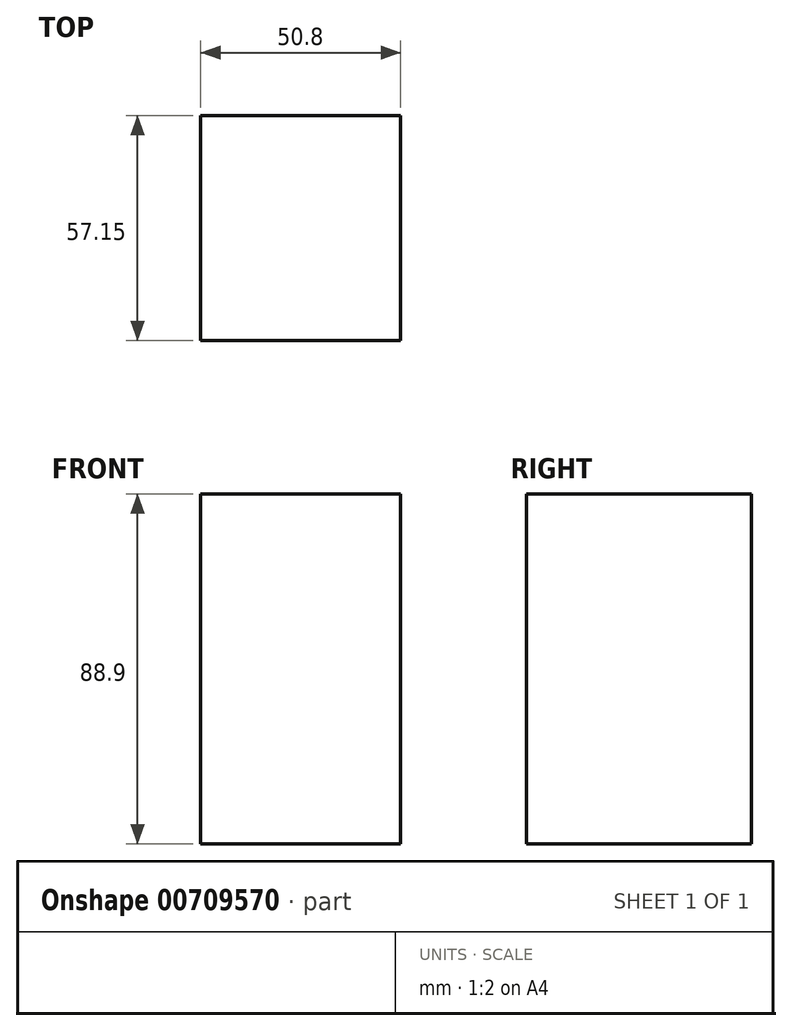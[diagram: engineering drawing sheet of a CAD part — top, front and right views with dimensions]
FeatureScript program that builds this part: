
annotation { "Feature Type Name" : "Feature", "Feature Type Description" : "" }
export const myFeature = defineFeature(function(context is Context, id is Id, definition is map)
    precondition{}
    {
        {
            var Q0;
            Q0=qCreatedBy(makeId("Front.planeOp"),FACE);
            var sketch = newSketch(context, id + "F0", { "sketchPlane" : qUnion([Q0])});
            skLineSegment(sketch, "E0.bottom", {"start": v(-36.59, 43.25) * mm, "end": v(14.21, 43.25) * mm});
            skLineSegment(sketch, "E0.top", {"start": v(-36.59, -45.65) * mm, "end": v(14.21, -45.65) * mm});
            skLineSegment(sketch, "E0.left", {"start": v(-36.59, 43.25) * mm, "end": v(-36.59, -45.65) * mm});
            skLineSegment(sketch, "E0.right", {"start": v(14.21, 43.25) * mm, "end": v(14.21, -45.65) * mm});
            skSolve(sketch);
        }
        {
            var Q0;
            Q0 = qSketchRegion(id + "F0", true);
            extrude(context, id + "F1", {"entities" : qUnion([Q0]), "depth" : 57.15 * mm, "offsetDistance" : 25.4 * mm});
        }
    });
